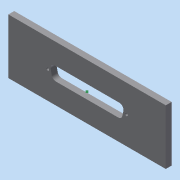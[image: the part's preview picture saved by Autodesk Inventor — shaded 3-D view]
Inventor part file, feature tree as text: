
AUTODESK INVENTOR PART (.ipt)
format: ipt  version: 2016 (Build 200138000, 138)  size: 221,696 bytes
history: native  units: in
note: dims shown in document units (in); Inventor stores cm internally (conversion verified against a paired STEP export)
features: sketch x3, extrude x2, projected_geometry x1
ambient origin geometry x8: Origin, YZ Plane, XZ Plane, XY Plane, X Axis, Y Axis, Z Axis, Center Point
bodies: Solid1 (feature_tree)
feature tree (6):
  extrude  "Extrusion1"  Depth=1.75in
  sketch  "Sketch2"  dims[d2=0.187in d3=0.0in d7=0.089in]
  extrude  "Extrusion2"  Depth=0.187in
  sketch  "Sketch1"  dims[d0=5.0in d1=1.75in]
  sketch  "Sketch3"  dims[d8=0.089in d9=2.5in d11=0.264in d13=0.264in d15=2.052in d16=1.983in d17=0.425in d20=0.21in d21=0.187in d22=0.0in d24=0.132in d25=0.132in]
  projected_geometry  "Projected Loop1"
